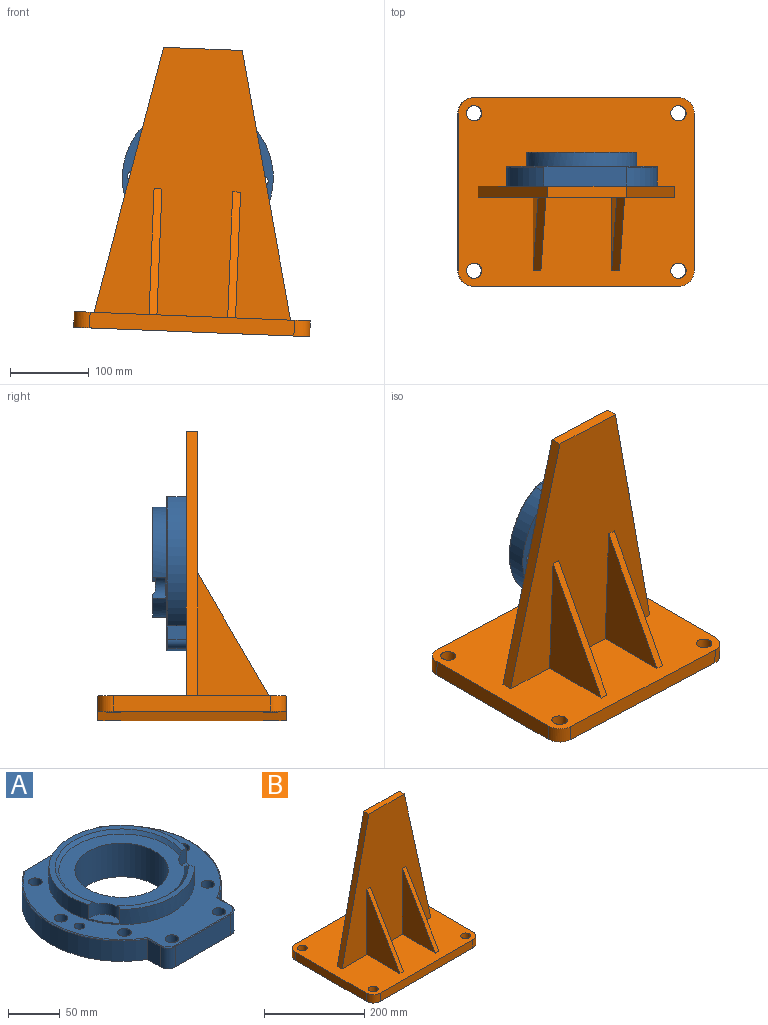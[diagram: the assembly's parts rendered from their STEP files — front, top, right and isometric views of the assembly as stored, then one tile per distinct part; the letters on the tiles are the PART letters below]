
ASSEMBLY  parts=2 mates=1
PART A: 38 faces, bbox 207.8x200.3x43 mm
  f0: cylinder r=96mm len=162.34mm, axis (0,0,-1), area 4648.3mm2, adj f2,f9,f13,f37
  f1: torus R=95mm, axis (0,0,1), area 308.7mm2, adj f8,f12,f31,f37
  f2: torus R=95mm, axis (0,0,1), area 304.3mm2, adj f0,f8,f28,f37
  f3: plane 140x91.89mm, normal (0,0,1), area 1526.2mm2, adj f6,f16,f33,f35
  f4: plane 101.6x27.21mm, normal (0,0,1), area 660.4mm2, adj f7,f16,f33,f35
  f5: plane 121x121mm, normal (0,0,1), area 5051.1mm2, adj f6,f7,f17,f33,f35
  f6: cone r=59mm half-angle=45deg, axis (0,0,1), area 1191.9mm2, adj f3,f5,f33,f35
  f7: cone r=59mm half-angle=45deg, axis (0,0,1), area 528.3mm2, adj f4,f5,f33,f35
  f8: plane 190.89x190mm, normal (0,0,1), area 12454.4mm2, adj f1,f2,f16,f18,f19,f20,f21,f22
  f9: plane 192x191.92mm, normal (0,0,-1), area 22018.7mm2, adj f0,f10,f11,f12,f13,f14,f15,f17
  f10: plane 74.86x24mm, normal (0,-1,0), area 1796.6mm2, adj f9,f14,f15,f30
  f11: plane 24x17.43mm, normal (1,0,0), area 418.3mm2, adj f9,f12,f14,f31
  f12: cylinder r=96mm len=163.92mm, axis (0,0,-1), area 4716.5mm2, adj f1,f9,f11,f37
  f13: plane 24x17.43mm, normal (-1,0,0), area 418.3mm2, adj f0,f9,f15,f28
  f14: cylinder r=10.57mm len=24mm, axis (0,0,1), area 398.6mm2, adj f9,f10,f11,f32
  f15: cylinder r=10.57mm len=24mm, axis (0,0,-1), area 398.6mm2, adj f9,f10,f13,f29
  f16: cylinder r=70mm len=140mm, axis (0,0,-1), area 6898.9mm2, adj f3,f4,f8,f33,f34,f35,f36
  f17: cylinder r=45mm len=90mm, axis (0,0,1), area 11168.4mm2, adj f5,f9
  f18: cylinder r=6.5mm len=25mm, axis (0,0,1), area 1021mm2, adj f8,f9
  f19: cylinder r=6.5mm len=25mm, axis (0,0,1), area 1021mm2, adj f8,f9
  f20: cylinder r=6.5mm len=25mm, axis (0,0,1), area 1021mm2, adj f8,f9
  f21: cylinder r=5.1mm len=25mm, axis (0,0,1), area 801.1mm2, adj f8,f9
  f22: cylinder r=6.5mm len=25mm, axis (0,0,1), area 1021mm2, adj f8,f9
  f23: cylinder r=6.5mm len=25mm, axis (0,0,1), area 1021mm2, adj f8,f9
  f24: cylinder r=6.5mm len=25mm, axis (0,0,1), area 1021mm2, adj f8,f9
  f25: cylinder r=5.1mm len=25mm, axis (0,0,1), area 801.1mm2, adj f8,f9
  f26: cylinder r=6.5mm len=25mm, axis (0,0,1), area 1021mm2, adj f8,f9
  f27: cylinder r=6.5mm len=25mm, axis (0,0,1), area 1021mm2, adj f8,f9
  f28: cylinder r=1mm len=18.01mm, axis (0,1,0), area 27.7mm2, adj f2,f8,f13,f29
  f29: torus R=9.57mm, axis (0,0,1), area 25.2mm2, adj f8,f15,f28,f30
  f30: cylinder r=1mm len=74.86mm, axis (-1,0,0), area 117.6mm2, adj f8,f10,f29,f32
  f31: cylinder r=1mm len=18.01mm, axis (0,-1,0), area 27.7mm2, adj f1,f8,f11,f32
  f32: torus R=9.57mm, axis (0,0,1), area 25.2mm2, adj f8,f14,f30,f31
  f33: cylinder r=16mm len=26.73mm, axis (0,0,1), area 588.8mm2, adj f3,f4,f5,f6,f7,f16,f34
  f34: plane 26.73x19.82mm, normal (0,0,1), area 289mm2, adj f16,f33
  f35: cylinder r=16mm len=26.73mm, axis (0,0,1), area 588.8mm2, adj f3,f4,f5,f6,f7,f16,f36
  f36: plane 26.73x19.82mm, normal (0,0,1), area 289mm2, adj f16,f35
  f37: plane 106.12x25mm, normal (-0.01,1,0), area 2652.5mm2, adj f0,f1,f2,f8,f9,f12
PART B: 25 faces, bbox 300x240x360 mm
  f0: plane 340x250mm, normal (0,-1,0), area 56300mm2, adj f1,f11,f12,f13,f15,f16,f17,f18
  f1: plane 300x240mm, normal (0,0,1), area 65102mm2, adj f0,f2,f3,f4,f5,f6,f7,f8
  f2: cylinder r=20mm len=20mm, axis (0,0,1), area 628.3mm2, adj f1,f3,f9,f10
  f3: plane 260x20mm, normal (0,1,0), area 5200mm2, adj f1,f2,f4,f10
  f4: cylinder r=20mm len=20mm, axis (0,0,1), area 628.3mm2, adj f1,f3,f5,f10
  f5: plane 200x20mm, normal (-1,0,0), area 4000mm2, adj f1,f4,f6,f10
  f6: cylinder r=20mm len=20mm, axis (0,0,1), area 628.3mm2, adj f1,f5,f7,f10
  f7: plane 260x20mm, normal (0,-1,0), area 5200mm2, adj f1,f6,f8,f10
  f8: cylinder r=20mm len=20mm, axis (0,0,1), area 628.3mm2, adj f1,f7,f9,f10
  f9: plane 200x20mm, normal (1,0,0), area 4000mm2, adj f1,f2,f8,f10
  f10: plane 300x240mm, normal (0,0,-1), area 70462mm2, adj f2,f3,f4,f5,f6,f7,f8,f9
  f11: plane 100x14mm, normal (0,0,1), area 1400mm2, adj f0,f12,f13,f14
  f12: plane 340x75mm, normal (-0.98,0,0.22), area 4874.4mm2, adj f0,f1,f11,f14
  f13: plane 340x75mm, normal (0.98,0,0.22), area 4874.4mm2, adj f0,f1,f11,f14
  f14: plane 340x250mm, normal (0,1,0), area 59500mm2, adj f1,f11,f12,f13
  f15: plane 160x93mm, normal (1,0,0), area 7440mm2, adj f0,f1,f17
  f16: plane 160x93mm, normal (-1,0,0), area 7440mm2, adj f0,f1,f17
  f17: plane 160x93mm, normal (0,-0.86,0.5), area 1850.6mm2, adj f0,f1,f15,f16
  f18: plane 160x93mm, normal (-1,0,0), area 7440mm2, adj f0,f1,f20
  f19: plane 160x93mm, normal (1,0,0), area 7440mm2, adj f0,f1,f20
  f20: plane 160x93mm, normal (0,-0.86,0.5), area 1850.6mm2, adj f0,f1,f18,f19
  f21: cylinder r=9.75mm len=20mm, axis (0,0,1), area 1225.2mm2, adj f1,f10
  f22: cylinder r=9.75mm len=20mm, axis (0,0,1), area 1225.2mm2, adj f1,f10
  f23: cylinder r=9.75mm len=20mm, axis (0,0,1), area 1225.2mm2, adj f1,f10
  f24: cylinder r=9.75mm len=20mm, axis (0,0,1), area 1225.2mm2, adj f1,f10
PLACE A rot(axis=(-0.01,-0.71,-0.71),178.4deg) t=(-25.91,6.69,169.35)mm
PLACE B rot(axis=(0,1,0),2.3deg) t=(-32.89,-0.31,-6.23)mm
MATE slider A.f0 <-> B.f14  axis (0,-1,0) through (-25.91,6.69,169.35)mm
